# Revit family: IEK_Держатель-зажим круглого проводника_6-12мм_Опорный_30-40мм
name_source: partatom
category: Обобщенные модели
units: mm (PartAtom-declared; Revit-internal decimal feet)

## family parameters
Может служить основой для арматурных стержней = Нет
Общий = Да
Основа = Грань
При загрузке вырезать с полостями = Нет
Размер круглого соединителя = Использовать диаметр
Тип детали = Нормальный
Точка расчета площади = Нет

## types (2) — shared parameters
ADSK_URL страницы изделия = https://www.iek.ru
ADSK_Версия Revit = 2019
ADSK_Версия семейства = 1.0
ADSK_Группирование = VIII. ЭЛЕМЕНТЫ ВНЕШНЕЙ МОЛНИЕЗАЩИТЫ
ADSK_Единица измерения = шт
ADSK_Завод-изготовитель = IEK
IEK_URL = https://www.iek.ru
IEK_Описание = Универсальная конструкция держателя позволяет использовать его с проводниками различной формы и габаритами.
zero-valued in all types: Отметка по умолчанию

## per-type parameters (varying)
| type | ADSK_Код изделия | ADSK_Масса | ADSK_Материал | ADSK_Материал наименование | ADSK_Наименование | IEK_Цена за единицу | KSI_CMa_Строительные материалы |
| 6-12_30-40_Сталь оцинкованная | ZHC81-11-1-16-040 | 0.12 | Сталь оцинкованная | Сталь оцинкованная | Дер.-заж. соед. кр. пров. 6-12мм оп. L=30-40мм оц. сталь IEK | 500 | 24.10.35.000.08.3.05.06-0001 |
| 6-12_30-40_Медь | ZHC81-50-1-16-040 | 0.13 | Медь | Медь | Дер.-заж. соед. кр. пров. 6-12мм оп. L=30-40мм медь IEK | 1008 | СТ 10 12 20 10 |
